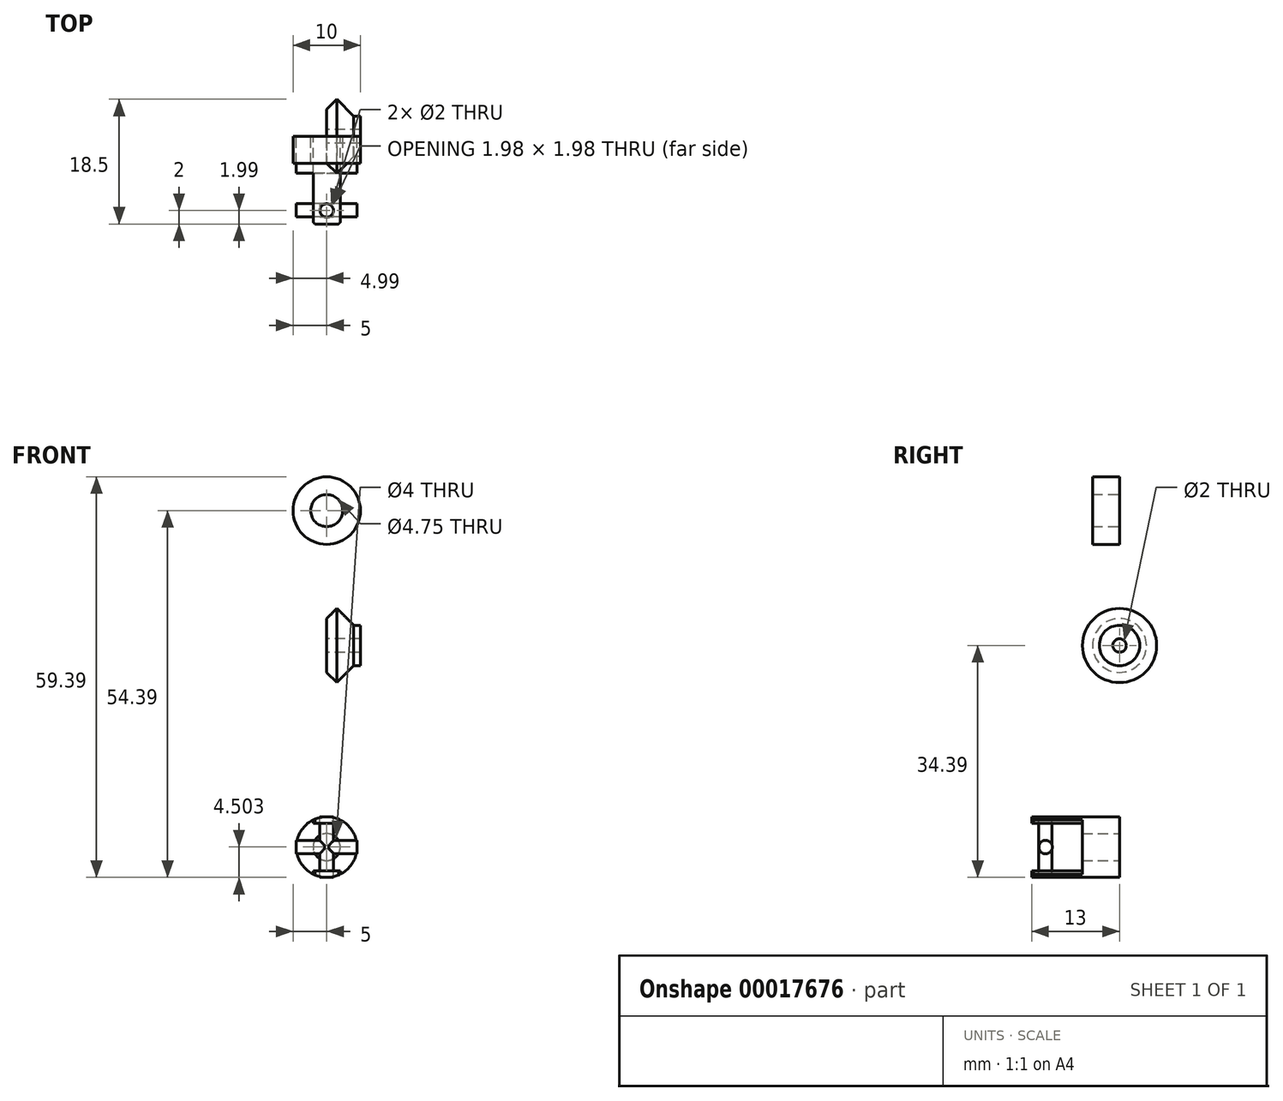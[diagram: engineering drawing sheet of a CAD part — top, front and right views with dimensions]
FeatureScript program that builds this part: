
annotation { "Feature Type Name" : "Feature", "Feature Type Description" : "" }
export const myFeature = defineFeature(function(context is Context, id is Id, definition is map)
    precondition{}
    {
        {
            var Q0;
            Q0=qCreatedBy(makeId("Front.planeOp"),FACE);
            var sketch = newSketch(context, id + "F0", { "sketchPlane" : qUnion([Q0])});
            skCircle(sketch, "E0", {"center": v(0, 0) * mm, "radius": 2.38 * mm});
            skCircle(sketch, "E1", {"center": v(0, 0) * mm, "radius": 5 * mm});
            skSolve(sketch);
        }
        {
            var Q0;
            Q0=makeQuery(id+"F0.imprint","IMPRINT",FACE,{"disambiguationData":[TD([[makeQuery(id+"F0.imprint","IMPRINT",EDGE,{"derivedFrom":sQuery(id+"F0.wireOp",EDGE,"E0")}),-1.0]])]});
            extrude(context, id + "F1", {"entities" : qUnion([Q0]), "depth" : 4 * mm});
        }
        {
            var Q0;
            Q0=qCreatedBy(makeId("Front.planeOp"),FACE);
            var sketch = newSketch(context, id + "F2", { "sketchPlane" : qUnion([Q0])});
            skLineSegment(sketch, "E2", {"start": v(-10.89, -20) * mm, "end": v(12.22, -20) * mm, "construction": true});
            skLineSegment(sketch, "E3", {"start": v(0, 0) * mm, "end": v(0, -20) * mm, "construction": true});
            skLineSegment(sketch, "E4", {"start": v(0, -19) * mm, "end": v(5, -19) * mm});
            skLineSegment(sketch, "E5", {"start": v(5, -19) * mm, "end": v(5, -17) * mm});
            skLineSegment(sketch, "E6", {"start": v(5, -17) * mm, "end": v(4, -17) * mm});
            skLineSegment(sketch, "E7", {"start": v(4, -17) * mm, "end": v(1.5, -14.5) * mm});
            skLineSegment(sketch, "E8", {"start": v(1.5, -14.5) * mm, "end": v(0, -16) * mm});
            skLineSegment(sketch, "E9", {"start": v(0, -16) * mm, "end": v(0, -19) * mm});
            skSolve(sketch);
        }
        {
            var Q0;
            Q0 = qSketchRegion(id + "F2", true);
            var Q1;
            Q1=sQuery(id+"F2.wireOp",EDGE,"E2");
            revolve(context, id + "F3", {"entities" : qUnion([Q0]), "axis" : qUnion([Q1]), "revolveType" : RevolveType.FULL});
        }
        {
            var Q0;
            Q0=qCreatedBy(makeId("Front.planeOp"),FACE);
            var sketch = newSketch(context, id + "F4", { "sketchPlane" : qUnion([Q0])});
            skCircle(sketch, "E10", {"center": v(0, -49.89) * mm, "radius": 4.5 * mm});
            skCircle(sketch, "E11", {"center": v(0, -49.89) * mm, "radius": 2 * mm});
            skSolve(sketch);
        }
        {
            var Q0;
            Q0 = qSketchRegion(id + "F4", true);
            extrude(context, id + "F5", {"entities" : qUnion([Q0]), "depth" : 13 * mm});
        }
        {
            var Q0;
            Q0=makeQuery(id+"F5.opExtrude","CAP_FACE",FACE,{"disambiguationData":[OSD([sQuery(id+"F4.wireOp",EDGE,"E10"),sQuery(id+"F4.wireOp",EDGE,"E11")])],"isStart":false});
            var sketch = newSketch(context, id + "F6", { "sketchPlane" : qUnion([Q0])});
            skLineSegment(sketch, "E12.bottom", {"start": v(-8, -46.39) * mm, "end": v(8, -46.39) * mm});
            skLineSegment(sketch, "E12.top", {"start": v(-8, -53.39) * mm, "end": v(8, -53.39) * mm});
            skLineSegment(sketch, "E12.left", {"start": v(-8, -46.39) * mm, "end": v(-8, -53.39) * mm});
            skLineSegment(sketch, "E12.right", {"start": v(8, -46.39) * mm, "end": v(8, -53.39) * mm});
            skLineSegment(sketch, "E13", {"start": v(0, -49.89) * mm, "end": v(10.8, -49.89) * mm, "construction": true});
            skSolve(sketch);
        }
        {
            var Q0;
            Q0 = qSketchRegion(id + "F6", true);
            extrude(context, id + "F7", {"entities" : qUnion([Q0]), "operationType" : NewBodyOperationType.REMOVE, "oppositeDirection" : true, "depth" : 7.5 * mm});
        }
        {
            var Q0;
            Q0=makeQuery(id+"F7.boolean.opBoolean","COPY",FACE,{"derivedFrom":makeQuery(id+"F7.opExtrude","SWEPT_FACE",FACE,{"disambiguationData":[OSD([sQuery(id+"F6.wireOp",EDGE,"E12.top")])]})});
            var sketch = newSketch(context, id + "F8", { "sketchPlane" : qUnion([Q0])});
            skLineSegment(sketch, "E14", {"start": v(0, -13) * mm, "end": v(0, -9.31) * mm, "construction": true});
            skCircle(sketch, "E15", {"center": v(0, -11) * mm, "radius": 1 * mm});
            skSolve(sketch);
        }
        {
            var Q0;
            Q0 = qSketchRegion(id + "F8", true);
            extrude(context, id + "F9", {"entities" : qUnion([Q0]), "operationType" : NewBodyOperationType.REMOVE, "oppositeDirection" : true, "depth" : 25 * mm, "hasSecondDirection" : true, "secondDirectionOppositeDirection" : false, "secondDirectionDepth" : 25 * mm});
        }
        {
            var Q0;
            Q0=makeQuery(id+"F7.boolean.opBoolean","COPY",FACE,{"derivedFrom":makeQuery(id+"F7.opExtrude","CAP_FACE",FACE,{"disambiguationData":[OSD([sQuery(id+"F6.wireOp",EDGE,"E12.bottom"),sQuery(id+"F6.wireOp",EDGE,"E12.top"),sQuery(id+"F6.wireOp",EDGE,"E12.left"),sQuery(id+"F6.wireOp",EDGE,"E12.right")])],"isStart":false})});
            var sketch = newSketch(context, id + "F10", { "sketchPlane" : qUnion([Q0])});
            skLineSegment(sketch, "E16.bottom", {"start": v(-2, -54.89) * mm, "end": v(-5, -54.89) * mm});
            skLineSegment(sketch, "E16.top", {"start": v(-2, -44.89) * mm, "end": v(-5, -44.89) * mm});
            skLineSegment(sketch, "E16.left", {"start": v(-2, -54.89) * mm, "end": v(-2, -44.89) * mm});
            skLineSegment(sketch, "E16.right", {"start": v(-5, -54.89) * mm, "end": v(-5, -44.89) * mm});
            skLineSegment(sketch, "E17.bottom", {"start": v(2, -54.89) * mm, "end": v(5, -54.89) * mm});
            skLineSegment(sketch, "E17.top", {"start": v(2, -44.89) * mm, "end": v(5, -44.89) * mm});
            skLineSegment(sketch, "E17.left", {"start": v(2, -54.89) * mm, "end": v(2, -44.89) * mm});
            skLineSegment(sketch, "E17.right", {"start": v(5, -54.89) * mm, "end": v(5, -44.89) * mm});
            skLineSegment(sketch, "E18", {"start": v(0, -49.89) * mm, "end": v(0, -58.24) * mm, "construction": true});
            skLineSegment(sketch, "E19", {"start": v(0, -49.89) * mm, "end": v(-3.54, -49.89) * mm, "construction": true});
            skSolve(sketch);
        }
        {
            var Q0;
            {var subQ8=sQuery(id+"F10.wireOp",EDGE,"E16.top");Q0=makeQuery(id+"F10.imprint","IMPRINT",FACE,{"disambiguationData":[TD([[makeQuery(id+"F10.imprint","IMPRINT",EDGE,{"derivedFrom":subQ8}),1.0]])]});}
            var Q1;
            {var subQ1=sQuery(id+"F6.wireOp",EDGE,"E12.top");var subQ5=makeQuery(id+"F7.boolean.opBoolean","COPY",EDGE,{"derivedFrom":makeQuery(id+"F7.opExtrude","CAP_EDGE",EDGE,{"disambiguationData":[OSD([subQ1])],"isStart":false})});var subQ9=sQuery(id+"F10.wireOp",EDGE,"E16.left");var subQ10=makeQuery(id+"F10.imprint","INTERSECT",VERTEX,{"derivedFrom":[subQ5,subQ9]});Q1=makeQuery(id+"F10.imprint","IMPRINT",FACE,{"disambiguationData":[TD([[makeQuery(id+"F10.imprint","IMPRINT",EDGE,{"disambiguationData":[TD([[subQ10,-1.0]])],"derivedFrom":subQ9}),1.0]])]});}
            var Q2;
            {var subQ1=sQuery(id+"F6.wireOp",EDGE,"E12.top");var subQ5=makeQuery(id+"F7.boolean.opBoolean","COPY",EDGE,{"derivedFrom":makeQuery(id+"F7.opExtrude","CAP_EDGE",EDGE,{"disambiguationData":[OSD([subQ1])],"isStart":false})});var subQ9=sQuery(id+"F10.wireOp",EDGE,"E17.left");var subQ10=makeQuery(id+"F10.imprint","INTERSECT",VERTEX,{"derivedFrom":[subQ5,subQ9]});Q2=makeQuery(id+"F10.imprint","IMPRINT",FACE,{"disambiguationData":[TD([[makeQuery(id+"F10.imprint","IMPRINT",EDGE,{"disambiguationData":[TD([[subQ10,-1.0]])],"derivedFrom":subQ9}),-1.0]])]});}
            var Q3;
            {var subQ6=sQuery(id+"F10.wireOp",EDGE,"E16.bottom");Q3=makeQuery(id+"F10.imprint","IMPRINT",FACE,{"disambiguationData":[TD([[makeQuery(id+"F10.imprint","IMPRINT",EDGE,{"derivedFrom":subQ6}),-1.0]])]});}
            var Q4;
            {var subQ8=sQuery(id+"F10.wireOp",EDGE,"E17.bottom");Q4=makeQuery(id+"F10.imprint","IMPRINT",FACE,{"disambiguationData":[TD([[makeQuery(id+"F10.imprint","IMPRINT",EDGE,{"derivedFrom":subQ8}),1.0]])]});}
            var Q5;
            {var subQ8=sQuery(id+"F10.wireOp",EDGE,"E17.top");Q5=makeQuery(id+"F10.imprint","IMPRINT",FACE,{"disambiguationData":[TD([[makeQuery(id+"F10.imprint","IMPRINT",EDGE,{"derivedFrom":subQ8}),-1.0]])]});}
            extrude(context, id + "F11", {"entities" : qUnion([Q0, Q1, Q2, Q3, Q4, Q5]), "operationType" : NewBodyOperationType.REMOVE, "depth" : 25 * mm});
        }
        {
            var Q0;
            {var subQ0=sQuery(id+"F4.wireOp",EDGE,"E10");Q0=makeQuery(id+"F11.boolean.opBoolean","INTERSECT",EDGE,{"derivedFrom":[makeQuery(id+"F7.boolean.opBoolean","SPLIT",FACE,{"disambiguationData":[TD([makeQuery(id+"F7.opExtrude","SWEPT_FACE",FACE,{"disambiguationData":[OSD([sQuery(id+"F6.wireOp",EDGE,"E12.top")])]})])],"derivedFrom":makeQuery(id+"F5.opExtrude","CAP_FACE",FACE,{"disambiguationData":[OSD([subQ0,sQuery(id+"F4.wireOp",EDGE,"E11")])],"isStart":false})}),makeQuery(id+"F11.opExtrude","SWEPT_FACE",FACE,{"disambiguationData":[OSD([sQuery(id+"F10.wireOp",EDGE,"E17.left")])]})]});}
            var Q1;
            {var subQ0=sQuery(id+"F4.wireOp",EDGE,"E10");Q1=makeQuery(id+"F11.boolean.opBoolean","INTERSECT",EDGE,{"derivedFrom":[makeQuery(id+"F7.boolean.opBoolean","SPLIT",FACE,{"disambiguationData":[TD([makeQuery(id+"F7.opExtrude","SWEPT_FACE",FACE,{"disambiguationData":[OSD([sQuery(id+"F6.wireOp",EDGE,"E12.top")])]})])],"derivedFrom":makeQuery(id+"F5.opExtrude","CAP_FACE",FACE,{"disambiguationData":[OSD([subQ0,sQuery(id+"F4.wireOp",EDGE,"E11")])],"isStart":false})}),makeQuery(id+"F11.opExtrude","SWEPT_FACE",FACE,{"disambiguationData":[OSD([sQuery(id+"F10.wireOp",EDGE,"E16.left")])]})]});}
            var Q2;
            {var subQ0=sQuery(id+"F4.wireOp",EDGE,"E10");Q2=makeQuery(id+"F11.boolean.opBoolean","INTERSECT",EDGE,{"derivedFrom":[makeQuery(id+"F7.boolean.opBoolean","SPLIT",FACE,{"disambiguationData":[TD([makeQuery(id+"F7.opExtrude","SWEPT_FACE",FACE,{"disambiguationData":[OSD([sQuery(id+"F6.wireOp",EDGE,"E12.bottom")])]})])],"derivedFrom":makeQuery(id+"F5.opExtrude","CAP_FACE",FACE,{"disambiguationData":[OSD([subQ0,sQuery(id+"F4.wireOp",EDGE,"E11")])],"isStart":false})}),makeQuery(id+"F11.opExtrude","SWEPT_FACE",FACE,{"disambiguationData":[OSD([sQuery(id+"F10.wireOp",EDGE,"E17.left")])]})]});}
            var Q3;
            {var subQ0=sQuery(id+"F4.wireOp",EDGE,"E10");Q3=makeQuery(id+"F11.boolean.opBoolean","INTERSECT",EDGE,{"derivedFrom":[makeQuery(id+"F7.boolean.opBoolean","SPLIT",FACE,{"disambiguationData":[TD([makeQuery(id+"F7.opExtrude","SWEPT_FACE",FACE,{"disambiguationData":[OSD([sQuery(id+"F6.wireOp",EDGE,"E12.bottom")])]})])],"derivedFrom":makeQuery(id+"F5.opExtrude","CAP_FACE",FACE,{"disambiguationData":[OSD([subQ0,sQuery(id+"F4.wireOp",EDGE,"E11")])],"isStart":false})}),makeQuery(id+"F11.opExtrude","SWEPT_FACE",FACE,{"disambiguationData":[OSD([sQuery(id+"F10.wireOp",EDGE,"E16.left")])]})]});}
            chamfer(context, id + "F12", {"entities" : qUnion([Q0, Q1, Q2, Q3]), "width" : 0.25 * mm, "tangentPropagation" : true});
        }
        {
            var Q0;
            Q0=makeQuery(id+"F7.boolean.opBoolean","COPY",FACE,{"derivedFrom":makeQuery(id+"F7.opExtrude","SWEPT_FACE",FACE,{"disambiguationData":[OSD([sQuery(id+"F6.wireOp",EDGE,"E12.bottom")])]})});
            cPlane(context, id + "F13", {"entities" : qUnion([Q0]), "cplaneType" : CPlaneType.OFFSET, "offset" : 3.5 * mm, "width" : 150 * mm, "height" : 150 * mm});
        }
        {
            var Q0;
            Q0=qCreatedBy(id+"F13.planeOp",FACE);
            var sketch = newSketch(context, id + "F14", { "sketchPlane" : qUnion([Q0])});
            skCircle(sketch, "E20", {"center": v(0, 11) * mm, "radius": 1 * mm});
            skSolve(sketch);
        }
        {
            var Q0;
            Q0 = qSketchRegion(id + "F14", true);
            extrude(context, id + "F15", {"entities" : qUnion([Q0]), "depth" : 4.5 * mm, "hasSecondDirection" : true, "secondDirectionOppositeDirection" : true, "secondDirectionDepth" : 4.5 * mm});
        }
        {
            var Q0;
            Q0=qCreatedBy(makeId("Right.planeOp"),FACE);
            var sketch = newSketch(context, id + "F16", { "sketchPlane" : qUnion([Q0])});
            skCircle(sketch, "E21", {"center": v(-10.95, -49.89) * mm, "radius": 1 * mm});
            skSolve(sketch);
        }
        {
            var Q0;
            Q0 = qSketchRegion(id + "F16", true);
            extrude(context, id + "F17", {"entities" : qUnion([Q0]), "operationType" : NewBodyOperationType.ADD, "depth" : 4.5 * mm, "hasSecondDirection" : true, "secondDirectionOppositeDirection" : true, "secondDirectionDepth" : 4.5 * mm});
        }
    });
